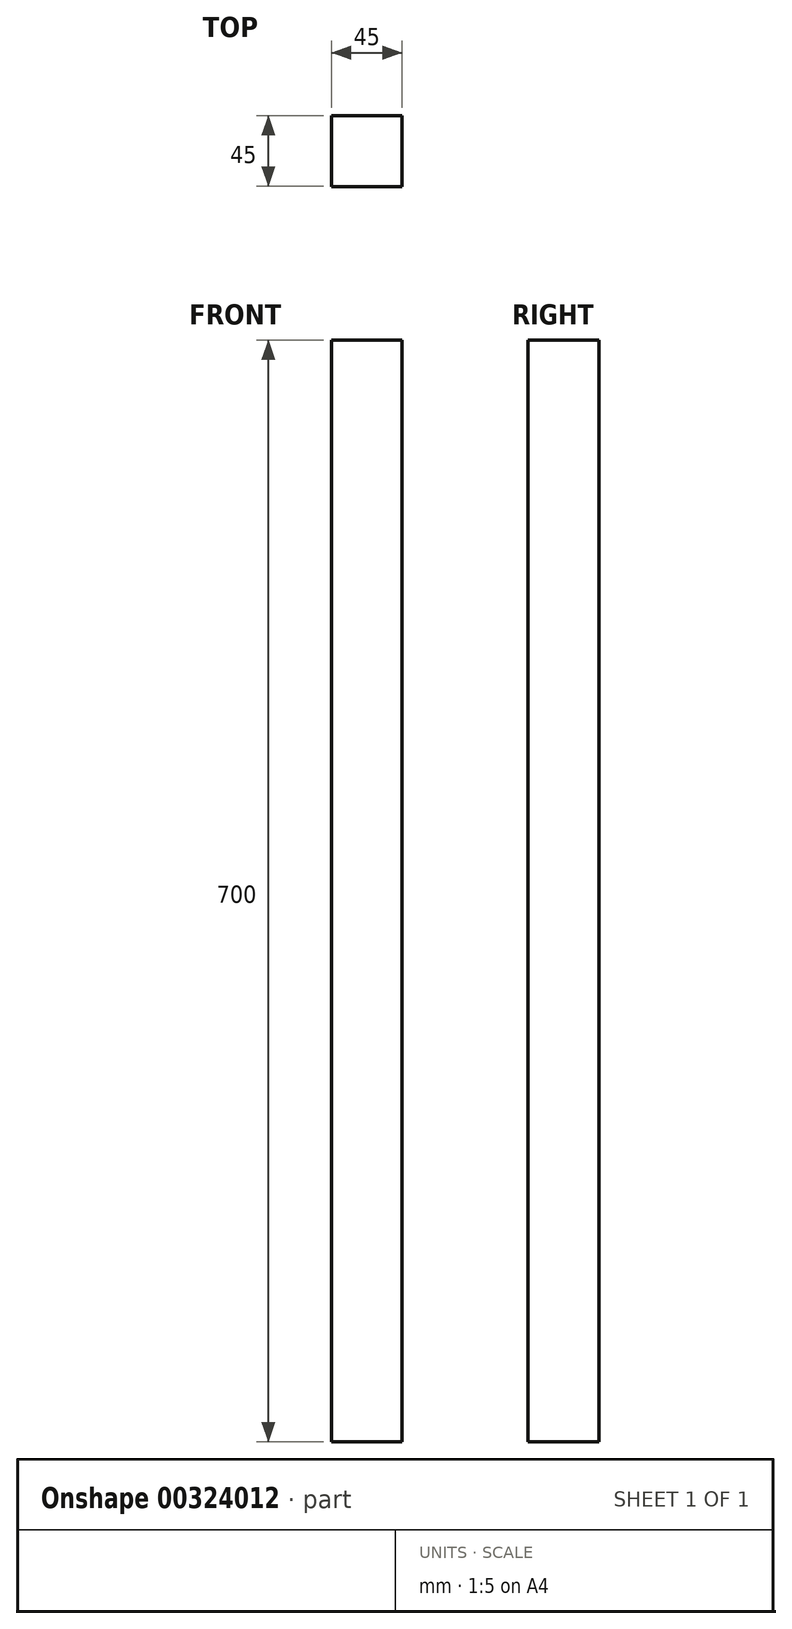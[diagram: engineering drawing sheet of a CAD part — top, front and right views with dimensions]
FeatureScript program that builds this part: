
annotation { "Feature Type Name" : "Feature", "Feature Type Description" : "" }
export const myFeature = defineFeature(function(context is Context, id is Id, definition is map)
    precondition{}
    {
        {
            var Q0;
            Q0=qCreatedBy(makeId("Top.planeOp"),FACE);
            var sketch = newSketch(context, id + "F0", { "sketchPlane" : qUnion([Q0])});
            skLineSegment(sketch, "E0.bottom", {"start": v(-30.85, 37.42) * mm, "end": v(14.15, 37.42) * mm});
            skLineSegment(sketch, "E0.top", {"start": v(-30.85, -7.58) * mm, "end": v(14.15, -7.58) * mm});
            skLineSegment(sketch, "E0.left", {"start": v(-30.85, 37.42) * mm, "end": v(-30.85, -7.58) * mm});
            skLineSegment(sketch, "E0.right", {"start": v(14.15, 37.42) * mm, "end": v(14.15, -7.58) * mm});
            skSolve(sketch);
        }
        {
            var Q0;
            Q0=makeQuery(id+"F0.imprint","IMPRINT",FACE,{"disambiguationData":[TD([[makeQuery(id+"F0.imprint","IMPRINT",EDGE,{"derivedFrom":sQuery(id+"F0.wireOp",EDGE,"E0.bottom")}),-1.0]])]});
            extrude(context, id + "F1", {"entities" : qUnion([Q0]), "depth" : 700 * mm});
        }
    });
